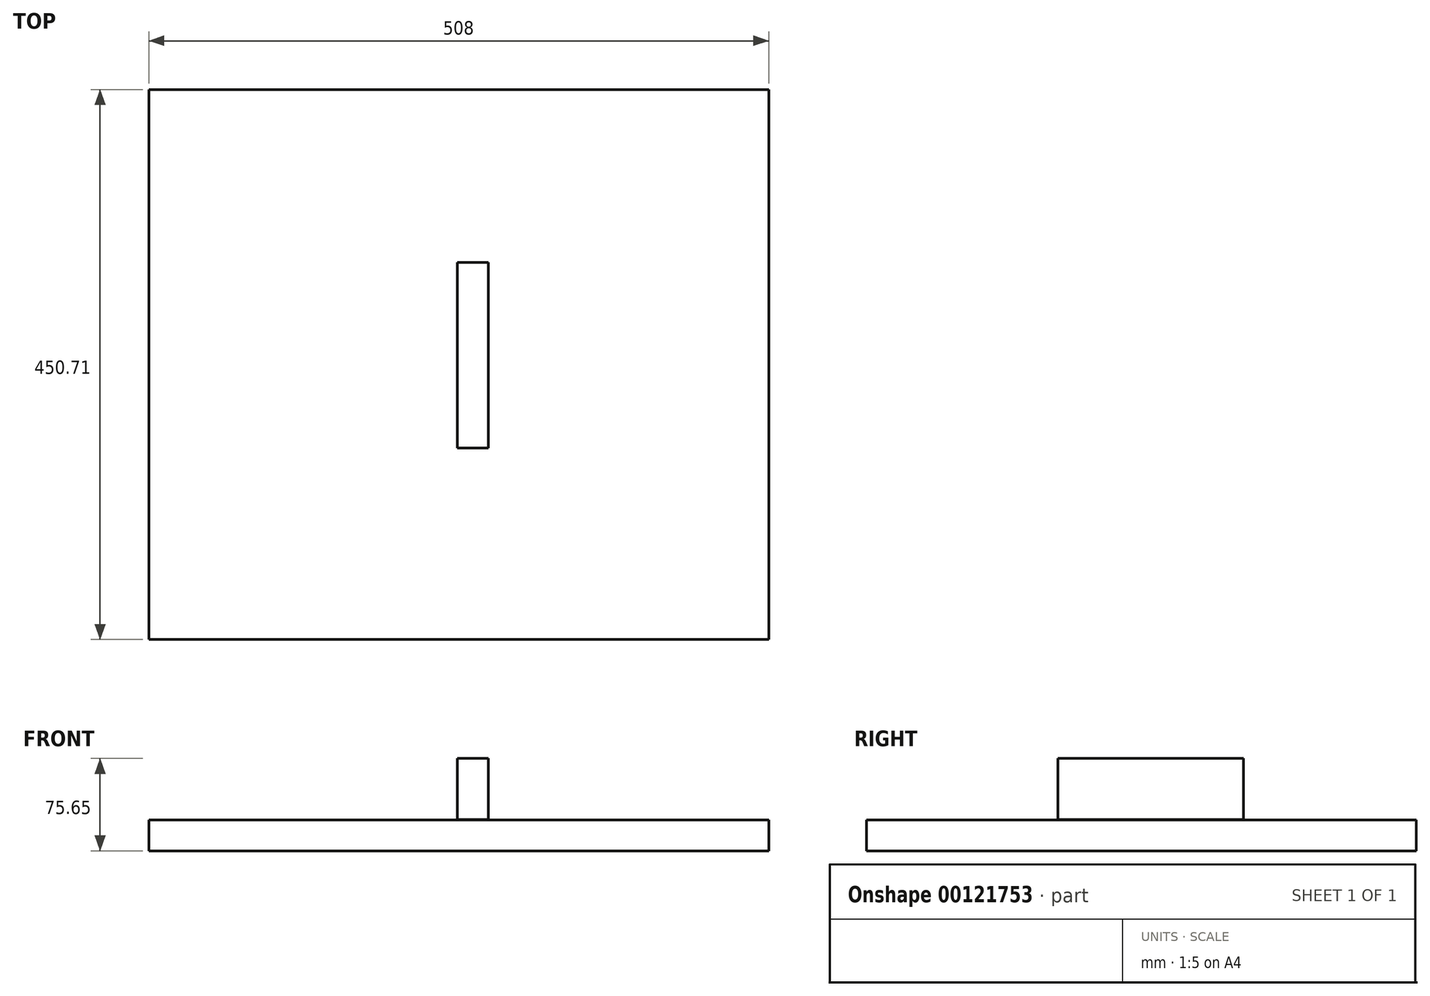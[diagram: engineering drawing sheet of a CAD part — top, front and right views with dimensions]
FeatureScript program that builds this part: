
annotation { "Feature Type Name" : "Feature", "Feature Type Description" : "" }
export const myFeature = defineFeature(function(context is Context, id is Id, definition is map)
    precondition{}
    {
        {
            var Q0;
            Q0=qCreatedBy(makeId("Top.planeOp"),FACE);
            var sketch = newSketch(context, id + "F0", { "sketchPlane" : qUnion([Q0])});
            skLineSegment(sketch, "E0.bottom", {"start": v(-252.83, 217.36) * mm, "end": v(255.17, 217.36) * mm});
            skLineSegment(sketch, "E0.top", {"start": v(-252.83, -233.35) * mm, "end": v(255.17, -233.35) * mm});
            skLineSegment(sketch, "E0.left", {"start": v(-252.83, 217.36) * mm, "end": v(-252.83, -233.35) * mm});
            skLineSegment(sketch, "E0.right", {"start": v(255.17, 217.36) * mm, "end": v(255.17, -233.35) * mm});
            skSolve(sketch);
        }
        {
            var Q0;
            Q0=makeQuery(id+"F0.imprint","IMPRINT",FACE,{"disambiguationData":[TD([[makeQuery(id+"F0.imprint","IMPRINT",EDGE,{"derivedFrom":sQuery(id+"F0.wireOp",EDGE,"E0.bottom")}),-1.0]])]});
            extrude(context, id + "F1", {"entities" : qUnion([Q0]), "depth" : 25.4 * mm});
        }
        {
            var Q0;
            Q0=qCreatedBy(makeId("Right.planeOp"),FACE);
            var sketch = newSketch(context, id + "F2", { "sketchPlane" : qUnion([Q0])});
            skLineSegment(sketch, "E1.bottom", {"start": v(75.65, 75.65) * mm, "end": v(-76.47, 75.65) * mm});
            skLineSegment(sketch, "E1.top", {"start": v(75.65, 25.63) * mm, "end": v(-76.47, 25.63) * mm});
            skLineSegment(sketch, "E1.left", {"start": v(75.65, 75.65) * mm, "end": v(75.65, 25.63) * mm});
            skLineSegment(sketch, "E1.right", {"start": v(-76.47, 75.65) * mm, "end": v(-76.47, 25.63) * mm});
            skSolve(sketch);
        }
        {
            var Q0;
            Q0 = qSketchRegion(id + "F2", true);
            extrude(context, id + "F3", {"entities" : qUnion([Q0]), "depth" : 25.4 * mm});
        }
    });
